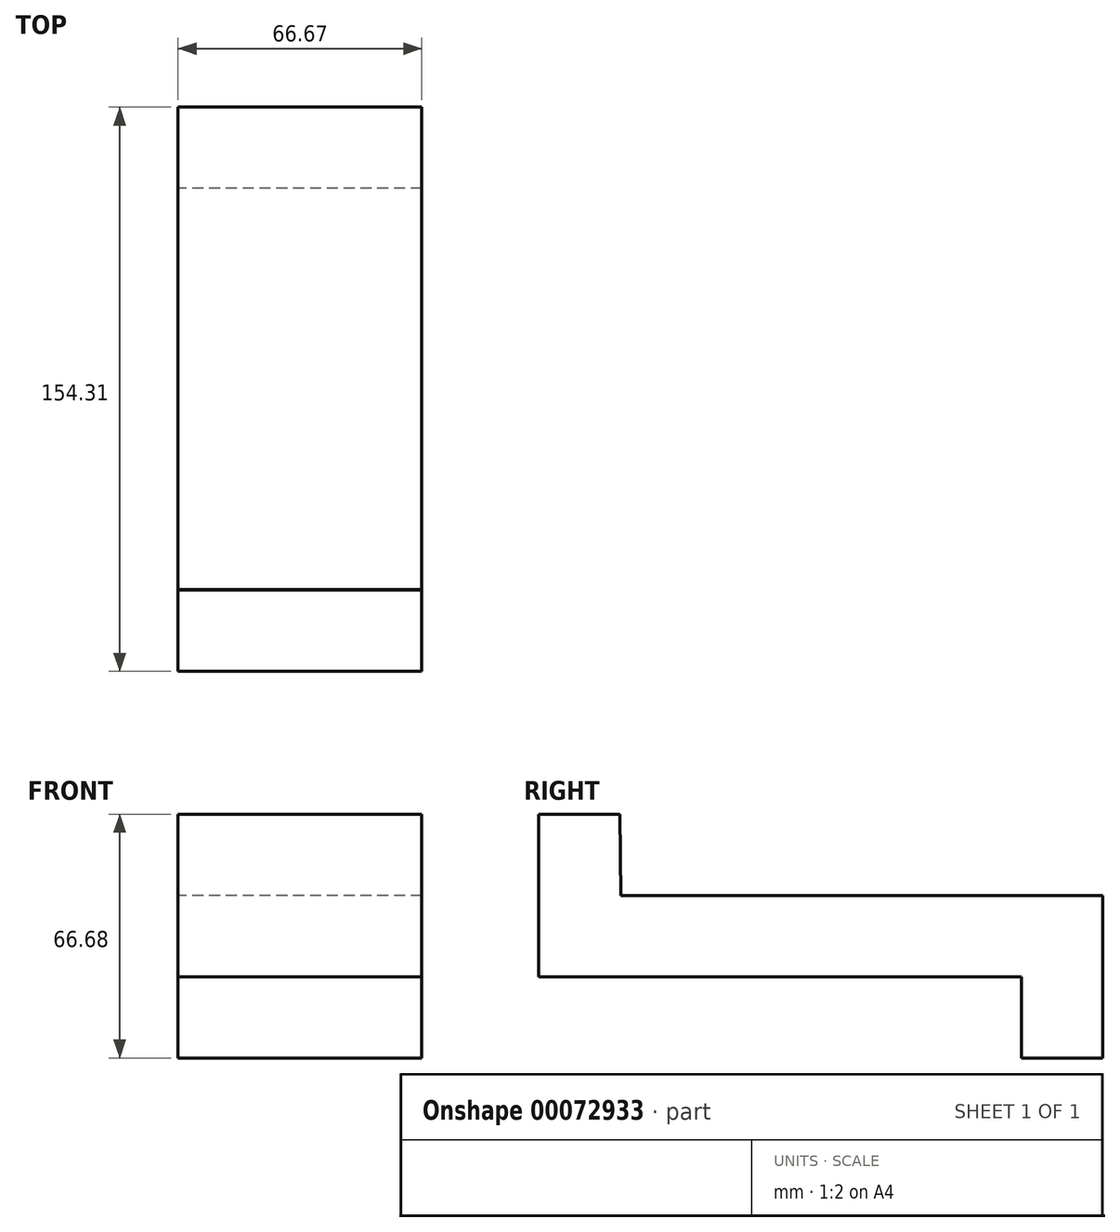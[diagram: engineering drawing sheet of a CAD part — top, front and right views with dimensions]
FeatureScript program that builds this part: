
annotation { "Feature Type Name" : "Feature", "Feature Type Description" : "" }
export const myFeature = defineFeature(function(context is Context, id is Id, definition is map)
    precondition{}
    {
        {
            var Q0;
            Q0=qCreatedBy(makeId("Right.planeOp"),FACE);
            var sketch = newSketch(context, id + "F0", { "sketchPlane" : qUnion([Q0])});
            skLineSegment(sketch, "E0", {"start": v(-154.26, 73.19) * mm, "end": v(-154.26, 28.74) * mm});
            skLineSegment(sketch, "E1", {"start": v(-154.26, 28.74) * mm, "end": v(-22.18, 28.74) * mm});
            skLineSegment(sketch, "E2", {"start": v(-22.18, 28.74) * mm, "end": v(-22.18, 6.51) * mm});
            skLineSegment(sketch, "E3", {"start": v(-22.18, 6.51) * mm, "end": v(0.05, 6.51) * mm});
            skLineSegment(sketch, "E4", {"start": v(0.05, 6.51) * mm, "end": v(0.05, 50.96) * mm});
            skLineSegment(sketch, "E5", {"start": v(0.05, 50.96) * mm, "end": v(-131.89, 50.96) * mm});
            skLineSegment(sketch, "E6", {"start": v(-154.26, 73.19) * mm, "end": v(-132.03, 73.19) * mm});
            skLineSegment(sketch, "E7", {"start": v(-132.03, 73.19) * mm, "end": v(-131.89, 50.96) * mm});
            skSolve(sketch);
        }
        {
            var Q0;
            Q0=makeQuery(id+"F0.imprint","IMPRINT",FACE,{"disambiguationData":[TD([[makeQuery(id+"F0.imprint","IMPRINT",EDGE,{"derivedFrom":sQuery(id+"F0.wireOp",EDGE,"E0")}),1.0]])]});
            var sketch = newSketch(context, id + "F1", { "sketchPlane" : qUnion([Q0])});
            skSolve(sketch);
        }
        {
            var Q0;
            Q0 = qSketchRegion(id + "F1", true);
            var Q1;
            Q1=makeQuery(id+"F0.imprint","IMPRINT",FACE,{"disambiguationData":[TD([[makeQuery(id+"F0.imprint","IMPRINT",EDGE,{"derivedFrom":sQuery(id+"F0.wireOp",EDGE,"E0")}),1.0]])]});
            extrude(context, id + "F2", {"entities" : qUnion([Q0, Q1]), "depth" : 66.67 * mm});
        }
    });
